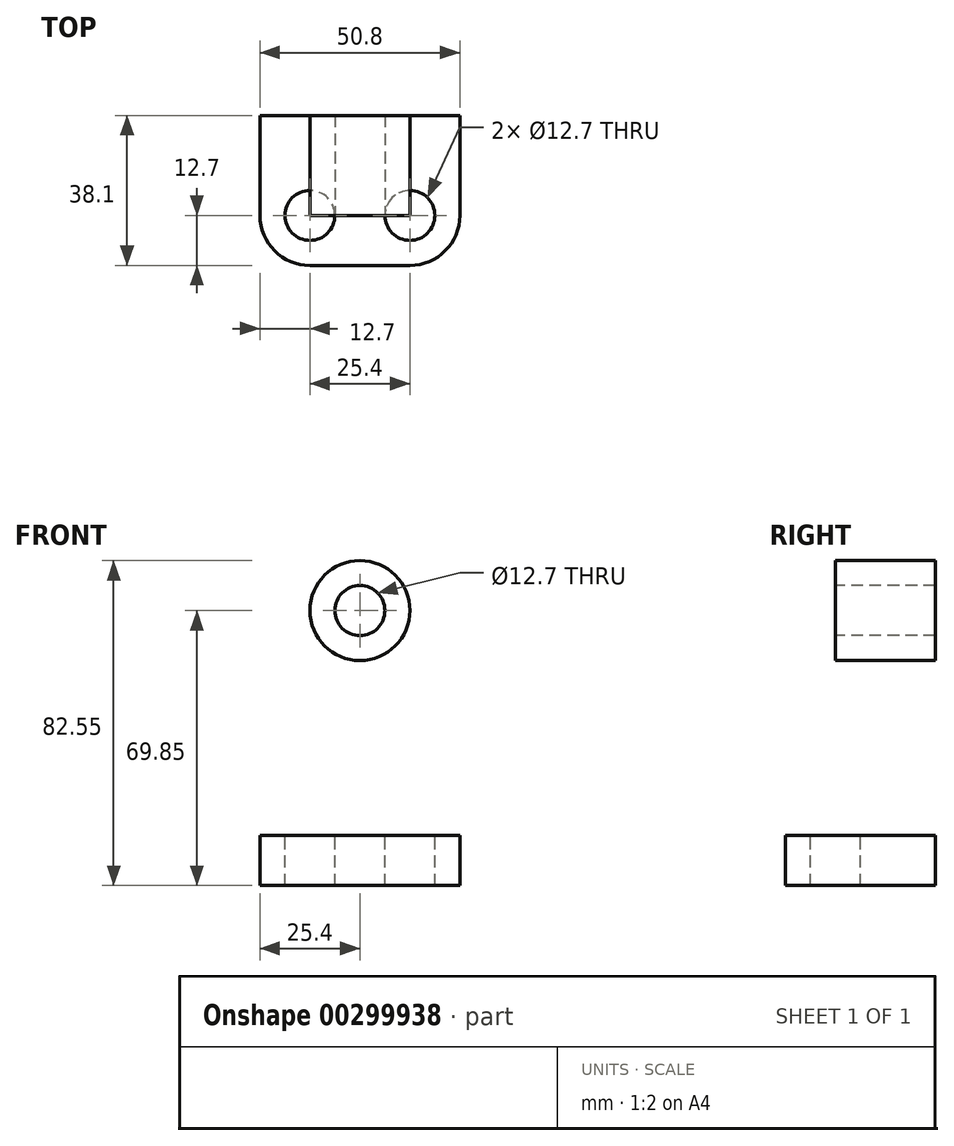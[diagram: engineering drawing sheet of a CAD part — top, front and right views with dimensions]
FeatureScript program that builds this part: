
annotation { "Feature Type Name" : "Feature", "Feature Type Description" : "" }
export const myFeature = defineFeature(function(context is Context, id is Id, definition is map)
    precondition{}
    {
        {
            var Q0;
            Q0=qCreatedBy(makeId("Top.planeOp"),FACE);
            var sketch = newSketch(context, id + "F0", { "sketchPlane" : qUnion([Q0])});
            skLineSegment(sketch, "E0.bottom", {"start": v(25.4, -19.05) * mm, "end": v(-25.4, -19.05) * mm});
            skLineSegment(sketch, "E0.top", {"start": v(25.4, 19.05) * mm, "end": v(-25.4, 19.05) * mm});
            skLineSegment(sketch, "E0.left", {"start": v(25.4, -19.05) * mm, "end": v(25.4, 19.05) * mm});
            skLineSegment(sketch, "E0.right", {"start": v(-25.4, -19.05) * mm, "end": v(-25.4, 19.05) * mm});
            skPoint(sketch, "E0.middle", {"position": v(0, 0) * mm});
            skSolve(sketch);
        }
        {
            var Q0;
            Q0=makeQuery(id+"F0.imprint","IMPRINT",FACE,{"disambiguationData":[TD([[makeQuery(id+"F0.imprint","IMPRINT",EDGE,{"derivedFrom":sQuery(id+"F0.wireOp",EDGE,"E0.bottom")}),-1.0]])]});
            extrude(context, id + "F1", {"entities" : qUnion([Q0]), "depth" : 12.7 * mm, "offsetDistance" : 25.4 * mm});
        }
        {
            var Q0;
            Q0=makeQuery(id+"F1.opExtrude","SWEPT_FACE",FACE,{"disambiguationData":[OSD([sQuery(id+"F0.wireOp",EDGE,"E0.top")])]});
            var sketch = newSketch(context, id + "F2", { "sketchPlane" : qUnion([Q0])});
            skLineSegment(sketch, "E1.bottom", {"start": v(-25.4, 12.7) * mm, "end": v(25.4, 12.7) * mm});
            skLineSegment(sketch, "E2.bottom", {"start": v(-12.7, 12.7) * mm, "end": v(12.7, 12.7) * mm});
            skLineSegment(sketch, "E2.left", {"start": v(-12.7, 26.05) * mm, "end": v(-12.7, 69.85) * mm});
            skLineSegment(sketch, "E2.right", {"start": v(12.7, 26.05) * mm, "end": v(12.7, 69.85) * mm});
            skArc(sketch, "E3", {"start": v(12.7, 26.05) * mm, "mid": v(17.33, 17.74) * mm, "end": v(25.4, 12.7) * mm});
            skCircle(sketch, "E4", {"center": v(0, 69.85) * mm, "radius": 12.7 * mm});
            skArc(sketch, "E5", {"start": v(-25.4, 12.7) * mm, "mid": v(-17.33, 17.74) * mm, "end": v(-12.7, 26.05) * mm});
            skSolve(sketch);
        }
        {
            var Q0;
            {var subQ1=sQuery(id+"F2.wireOp",EDGE,"E2.bottom");Q0=makeQuery(id+"F2.imprint","IMPRINT",FACE,{"disambiguationData":[TD([[makeQuery(id+"F2.imprint","IMPRINT",EDGE,{"derivedFrom":subQ1}),1.0]])]});}
            var Q1;
            {var subQ0=sQuery(id+"F2.wireOp",EDGE,"E4");var subQ1=makeQuery(id+"F2.imprint","INTERSECT",VERTEX,{"derivedFrom":[sQuery(id+"F2.wireOp",EDGE,"E2.left"),subQ0]});Q1=makeQuery(id+"F2.imprint","IMPRINT",FACE,{"disambiguationData":[TD([[makeQuery(id+"F2.imprint","IMPRINT",EDGE,{"disambiguationData":[TD([[subQ1,1.0]])],"derivedFrom":subQ0}),1.0]])]});}
            extrude(context, id + "F3", {"entities" : qUnion([Q0, Q1]), "operationType" : NewBodyOperationType.ADD, "oppositeDirection" : true, "depth" : 12.7 * mm, "offsetDistance" : 25.4 * mm});
        }
        {
            var Q0;
            Q0=makeQuery(id+"F3.opExtrude","CAP_FACE",FACE,{"disambiguationData":[OSD([sQuery(id+"F2.wireOp",EDGE,"E1.bottom"),sQuery(id+"F2.wireOp",EDGE,"E2.bottom"),sQuery(id+"F2.wireOp",EDGE,"E2.left"),sQuery(id+"F2.wireOp",EDGE,"E2.right"),sQuery(id+"F2.wireOp",EDGE,"E3"),sQuery(id+"F2.wireOp",EDGE,"E4"),sQuery(id+"F2.wireOp",EDGE,"E5")])],"isStart":false});
            var sketch = newSketch(context, id + "F4", { "sketchPlane" : qUnion([Q0])});
            skCircle(sketch, "E6", {"center": v(0, 69.85) * mm, "radius": 12.7 * mm});
            skSolve(sketch);
        }
        {
            var Q0;
            {var subQ0=sQuery(id+"F4.wireOp",EDGE,"E6");Q0=makeQuery(id+"F4.imprint","IMPRINT",FACE,{"disambiguationData":[TD([[makeQuery(id+"F4.imprint","IMPRINT",EDGE,{"disambiguationData":[OD(0.0)],"derivedFrom":subQ0}),-1.0]])]});}
            extrude(context, id + "F5", {"entities" : qUnion([Q0]), "operationType" : NewBodyOperationType.ADD, "depth" : 12.7 * mm, "offsetDistance" : 25.4 * mm});
        }
        {
            var Q0;
            Q0=makeQuery(id+"F5.opExtrude","CAP_FACE",FACE,{"disambiguationData":[OSD([sQuery(id+"F4.wireOp",EDGE,"E6")])],"isStart":false});
            var sketch = newSketch(context, id + "F6", { "sketchPlane" : qUnion([Q0])});
            skCircle(sketch, "E7.0", {"center": v(0, 69.85) * mm, "radius": 6.35 * mm});
            skSolve(sketch);
        }
        {
            var Q0;
            Q0=makeQuery(id+"F6.imprint","IMPRINT",FACE,{"disambiguationData":[TD([[makeQuery(id+"F6.imprint","IMPRINT",EDGE,{"derivedFrom":sQuery(id+"F6.wireOp",EDGE,"E7.0")}),1.0]])]});
            var Q1;
            Q1=sQuery(id+"F6.wireOp",EDGE,"E7.0");
            extrude(context, id + "F7", {"entities" : qUnion([Q0]), "operationType" : NewBodyOperationType.REMOVE, "surfaceEntities" : qUnion([Q1]), "endBound" : BoundingType.THROUGH_ALL, "oppositeDirection" : true, "depth" : 25.4 * mm, "offsetDistance" : 25.4 * mm});
        }
        {
            var Q0;
            Q0=makeQuery(id+"F1.opExtrude","CAP_FACE",FACE,{"disambiguationData":[OSD([sQuery(id+"F0.wireOp",EDGE,"E0.bottom"),sQuery(id+"F0.wireOp",EDGE,"E0.top"),sQuery(id+"F0.wireOp",EDGE,"E0.left"),sQuery(id+"F0.wireOp",EDGE,"E0.right")])],"isStart":false});
            var sketch = newSketch(context, id + "F8", { "sketchPlane" : qUnion([Q0])});
            skCircle(sketch, "E8", {"center": v(-12.7, -6.35) * mm, "radius": 6.35 * mm});
            skCircle(sketch, "E9", {"center": v(12.7, -6.35) * mm, "radius": 6.35 * mm});
            skSolve(sketch);
        }
        {
            var Q0;
            Q0=makeQuery(id+"F8.imprint","IMPRINT",FACE,{"disambiguationData":[TD([[makeQuery(id+"F8.imprint","IMPRINT",EDGE,{"derivedFrom":sQuery(id+"F8.wireOp",EDGE,"E8")}),1.0]])]});
            var Q1;
            Q1=makeQuery(id+"F8.imprint","IMPRINT",FACE,{"disambiguationData":[TD([[makeQuery(id+"F8.imprint","IMPRINT",EDGE,{"derivedFrom":sQuery(id+"F8.wireOp",EDGE,"E9")}),1.0]])]});
            extrude(context, id + "F9", {"entities" : qUnion([Q0, Q1]), "operationType" : NewBodyOperationType.REMOVE, "endBound" : BoundingType.THROUGH_ALL, "oppositeDirection" : true, "depth" : 25.4 * mm, "offsetDistance" : 25.4 * mm});
        }
        {
            var Q0;
            Q0=makeQuery(id+"F1.opExtrude","SWEPT_EDGE",EDGE,{"disambiguationData":[OSD([sQuery(id+"F0.wireOp",EDGE,"E0.bottom"),sQuery(id+"F0.wireOp",EDGE,"E0.right")])]});
            var Q1;
            Q1=makeQuery(id+"F1.opExtrude","SWEPT_EDGE",EDGE,{"disambiguationData":[OSD([sQuery(id+"F0.wireOp",EDGE,"E0.bottom"),sQuery(id+"F0.wireOp",EDGE,"E0.left")])]});
            fillet(context, id + "F10", {"entities" : qUnion([Q0, Q1]), "radius" : 12.7 * mm, "tangentPropagation" : true, "allowEdgeOverflow" : false});
        }
    });
